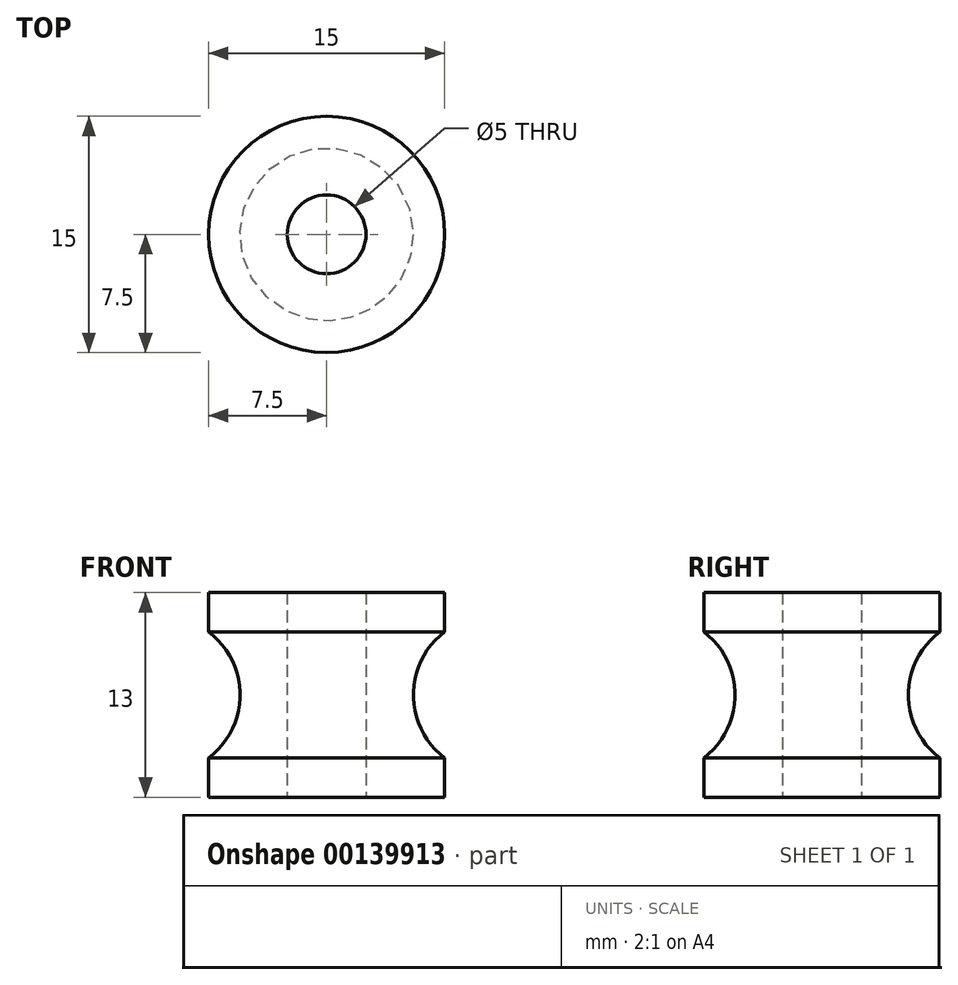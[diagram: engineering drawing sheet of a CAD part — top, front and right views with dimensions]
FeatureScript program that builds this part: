
annotation { "Feature Type Name" : "Feature", "Feature Type Description" : "" }
export const myFeature = defineFeature(function(context is Context, id is Id, definition is map)
    precondition{}
    {
        {
            var Q0;
            Q0=qCreatedBy(makeId("Top.planeOp"),FACE);
            var sketch = newSketch(context, id + "F0", { "sketchPlane" : qUnion([Q0])});
            skCircle(sketch, "E0", {"center": v(0, 0) * mm, "radius": 7.5 * mm});
            skCircle(sketch, "E1", {"center": v(0, 0) * mm, "radius": 2.5 * mm});
            skSolve(sketch);
        }
        {
            var Q0;
            Q0 = qSketchRegion(id + "F0", true);
            extrude(context, id + "F1", {"entities" : qUnion([Q0]), "depth" : 13 * mm});
        }
        {
            var Q0;
            Q0=qCreatedBy(makeId("Top.planeOp"),FACE);
            cPlane(context, id + "F2", {"entities" : qUnion([Q0]), "cplaneType" : CPlaneType.OFFSET, "offset" : 6.5 * mm, "width" : 150 * mm, "height" : 150 * mm});
        }
        {
            var Q0;
            Q0=qCreatedBy(id+"F2.planeOp",FACE);
            var sketch = newSketch(context, id + "F3", { "sketchPlane" : qUnion([Q0])});
            skCircle(sketch, "E2", {"center": v(0, 0) * mm, "radius": 5.5 * mm});
            skSolve(sketch);
        }
        {
            var Q0;
            Q0=qCreatedBy(makeId("Top.planeOp"),FACE);
            cPlane(context, id + "F4", {"entities" : qUnion([Q0]), "cplaneType" : CPlaneType.OFFSET, "offset" : 2.5 * mm, "width" : 150 * mm, "height" : 150 * mm});
        }
        {
            var Q0;
            Q0=qCreatedBy(id+"F4.planeOp",FACE);
            var sketch = newSketch(context, id + "F5", { "sketchPlane" : qUnion([Q0])});
            skCircle(sketch, "E3.0", {"center": v(0, 0) * mm, "radius": 7.5 * mm});
            skSolve(sketch);
        }
        {
            var Q0;
            Q0=makeQuery(id+"F1.opExtrude","CAP_FACE",FACE,{"disambiguationData":[OSD([sQuery(id+"F0.wireOp",EDGE,"E0"),sQuery(id+"F0.wireOp",EDGE,"E1")])],"isStart":false});
            cPlane(context, id + "F6", {"entities" : qUnion([Q0]), "cplaneType" : CPlaneType.OFFSET, "offset" : 2.5 * mm, "oppositeDirection" : true, "width" : 150 * mm, "height" : 150 * mm});
        }
        {
            var Q0;
            Q0=qCreatedBy(id+"F6.planeOp",FACE);
            var sketch = newSketch(context, id + "F7", { "sketchPlane" : qUnion([Q0])});
            skCircle(sketch, "E4.0", {"center": v(0, 0) * mm, "radius": 7.5 * mm});
            skSolve(sketch);
        }
        {
            var Q0;
            Q0=qCreatedBy(makeId("Front.planeOp"),FACE);
            var sketch = newSketch(context, id + "F8", { "sketchPlane" : qUnion([Q0])});
            skLineSegment(sketch, "E5.0", {"start": v(-7.5, 10.5) * mm, "end": v(7.5, 10.5) * mm, "construction": true});
            skLineSegment(sketch, "E6.0", {"start": v(-5.5, 6.5) * mm, "end": v(5.5, 6.5) * mm, "construction": true});
            skLineSegment(sketch, "E7.0", {"start": v(-7.5, 2.5) * mm, "end": v(7.5, 2.5) * mm, "construction": true});
            skArc(sketch, "E8", {"start": v(7.5, 10.5) * mm, "mid": v(5.5, 6.5) * mm, "end": v(7.5, 2.5) * mm});
            skLineSegment(sketch, "E9", {"start": v(7.5, 10.5) * mm, "end": v(7.5, 2.5) * mm});
            skSolve(sketch);
        }
        {
            var Q0;
            Q0 = qSketchRegion(id + "F8", true);
            var Q1;
            Q1 = qConstructionFilter(qBodyType(qCreatedBy(id + "F3" ,EDGE), BodyType.WIRE), ConstructionObject.NO);
            sweep(context, id + "F9", {"operationType" : NewBodyOperationType.REMOVE, "profiles" : qUnion([Q0]), "path" : qUnion([Q1])});
        }
    });
